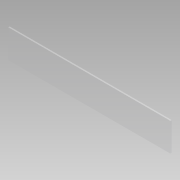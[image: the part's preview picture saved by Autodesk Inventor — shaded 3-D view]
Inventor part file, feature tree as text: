
AUTODESK INVENTOR PART (.ipt)
format: ipt  version: 2012 (Build 160160000, 160)  size: 66,048 bytes
history: native  units: in
note: dims shown in document units (in); Inventor stores cm internally (conversion verified against a paired STEP export)
features: extrude x1, sketch x1
ambient origin geometry x8: Origin, YZ Plane, XZ Plane, XY Plane, X Axis, Y Axis, Z Axis, Center Point
bodies: Solid1 (feature_tree)
feature tree (2):
  extrude  "Extrusion1"  Depth=5.0in
  sketch  "Sketch1"  dims[d0=28.628in d1=5.0in d2=0.25in d3=0.0in]
